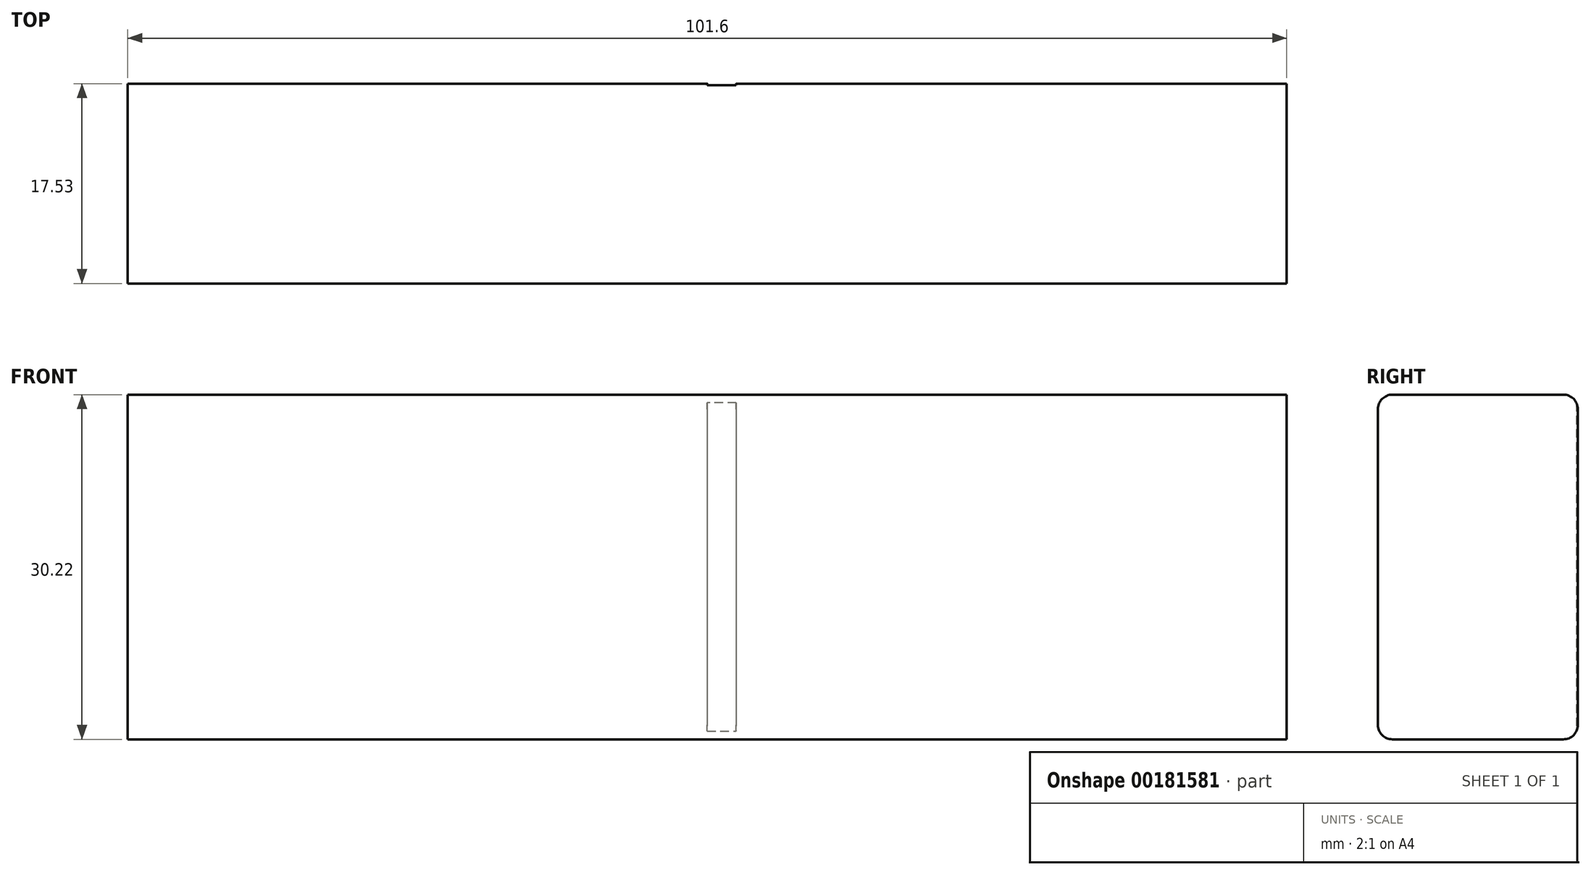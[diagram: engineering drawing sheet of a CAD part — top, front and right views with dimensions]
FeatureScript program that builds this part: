
annotation { "Feature Type Name" : "Feature", "Feature Type Description" : "" }
export const myFeature = defineFeature(function(context is Context, id is Id, definition is map)
    precondition{}
    {
        {
            var Q0;
            Q0=qCreatedBy(makeId("Right.planeOp"),FACE);
            var sketch = newSketch(context, id + "F0", { "sketchPlane" : qUnion([Q0])});
            skLineSegment(sketch, "E0.bottom", {"start": v(-17.87, 27.97) * mm, "end": v(-0.34, 27.97) * mm});
            skLineSegment(sketch, "E0.top", {"start": v(-17.87, -2.25) * mm, "end": v(-0.34, -2.25) * mm});
            skLineSegment(sketch, "E0.left", {"start": v(-17.87, 27.97) * mm, "end": v(-17.87, -2.25) * mm});
            skLineSegment(sketch, "E0.right", {"start": v(-0.34, 27.97) * mm, "end": v(-0.34, -2.25) * mm});
            skSolve(sketch);
        }
        {
            var Q0;
            Q0=makeQuery(id+"F0.imprint","IMPRINT",FACE,{"disambiguationData":[TD([[makeQuery(id+"F0.imprint","IMPRINT",EDGE,{"derivedFrom":sQuery(id+"F0.wireOp",EDGE,"E0.bottom")}),-1.0]])]});
            extrude(context, id + "F1", {"entities" : qUnion([Q0]), "depth" : 101.6 * mm});
        }
        {
            var Q0;
            Q0=makeQuery(id+"F1.opExtrude","SWEPT_FACE",FACE,{"disambiguationData":[OSD([sQuery(id+"F0.wireOp",EDGE,"E0.right")])]});
            var sketch = newSketch(context, id + "F2", { "sketchPlane" : qUnion([Q0])});
            skLineSegment(sketch, "E1", {"start": v(-50.8, 27.97) * mm, "end": v(-50.8, -2.25) * mm});
            skLineSegment(sketch, "E2", {"start": v(-53.34, 27.97) * mm, "end": v(-53.34, -2.25) * mm});
            skSolve(sketch);
        }
        {
            var Q0;
            {var subQ0=sQuery(id+"F2.wireOp",EDGE,"E1");Q0=makeQuery(id+"F2.imprint","IMPRINT",FACE,{"disambiguationData":[TD([[makeQuery(id+"F2.imprint","IMPRINT",EDGE,{"derivedFrom":subQ0}),-1.0]])]});}
            extrude(context, id + "F3", {"entities" : qUnion([Q0]), "operationType" : NewBodyOperationType.REMOVE, "oppositeDirection" : true, "depth" : 0.13 * mm});
        }
        {
            var Q0;
            {var subQ0=sQuery(id+"F0.wireOp",EDGE,"E0.bottom");var subQ1=sQuery(id+"F0.wireOp",EDGE,"E0.right");Q0=makeQuery(id+"F3.boolean.opBoolean","SPLIT",EDGE,{"disambiguationData":[TD([makeQuery(id+"F3.opExtrude","SWEPT_FACE",FACE,{"disambiguationData":[OSD([sQuery(id+"F2.wireOp",EDGE,"E2")])]})])],"derivedFrom":makeQuery(id+"F1.opExtrude","SWEPT_EDGE",EDGE,{"disambiguationData":[OSD([subQ0,subQ1])]})});}
            var Q1;
            Q1=makeQuery(id+"F1.opExtrude","SWEPT_EDGE",EDGE,{"disambiguationData":[OSD([sQuery(id+"F0.wireOp",EDGE,"E0.bottom"),sQuery(id+"F0.wireOp",EDGE,"E0.left")])]});
            var Q2;
            Q2=makeQuery(id+"F1.opExtrude","SWEPT_EDGE",EDGE,{"disambiguationData":[OSD([sQuery(id+"F0.wireOp",EDGE,"E0.top"),sQuery(id+"F0.wireOp",EDGE,"E0.left")])]});
            var Q3;
            {var subQ0=sQuery(id+"F0.wireOp",EDGE,"E0.right");var subQ1=sQuery(id+"F0.wireOp",EDGE,"E0.top");Q3=makeQuery(id+"F3.boolean.opBoolean","SPLIT",EDGE,{"disambiguationData":[TD([makeQuery(id+"F3.opExtrude","SWEPT_FACE",FACE,{"disambiguationData":[OSD([sQuery(id+"F2.wireOp",EDGE,"E1")])]})])],"derivedFrom":makeQuery(id+"F1.opExtrude","SWEPT_EDGE",EDGE,{"disambiguationData":[OSD([subQ1,subQ0])]})});}
            fillet(context, id + "F4", {"entities" : qUnion([Q0, Q1, Q2, Q3]), "radius" : 1.27 * mm, "tangentPropagation" : true, "allowEdgeOverflow" : false});
        }
    });
